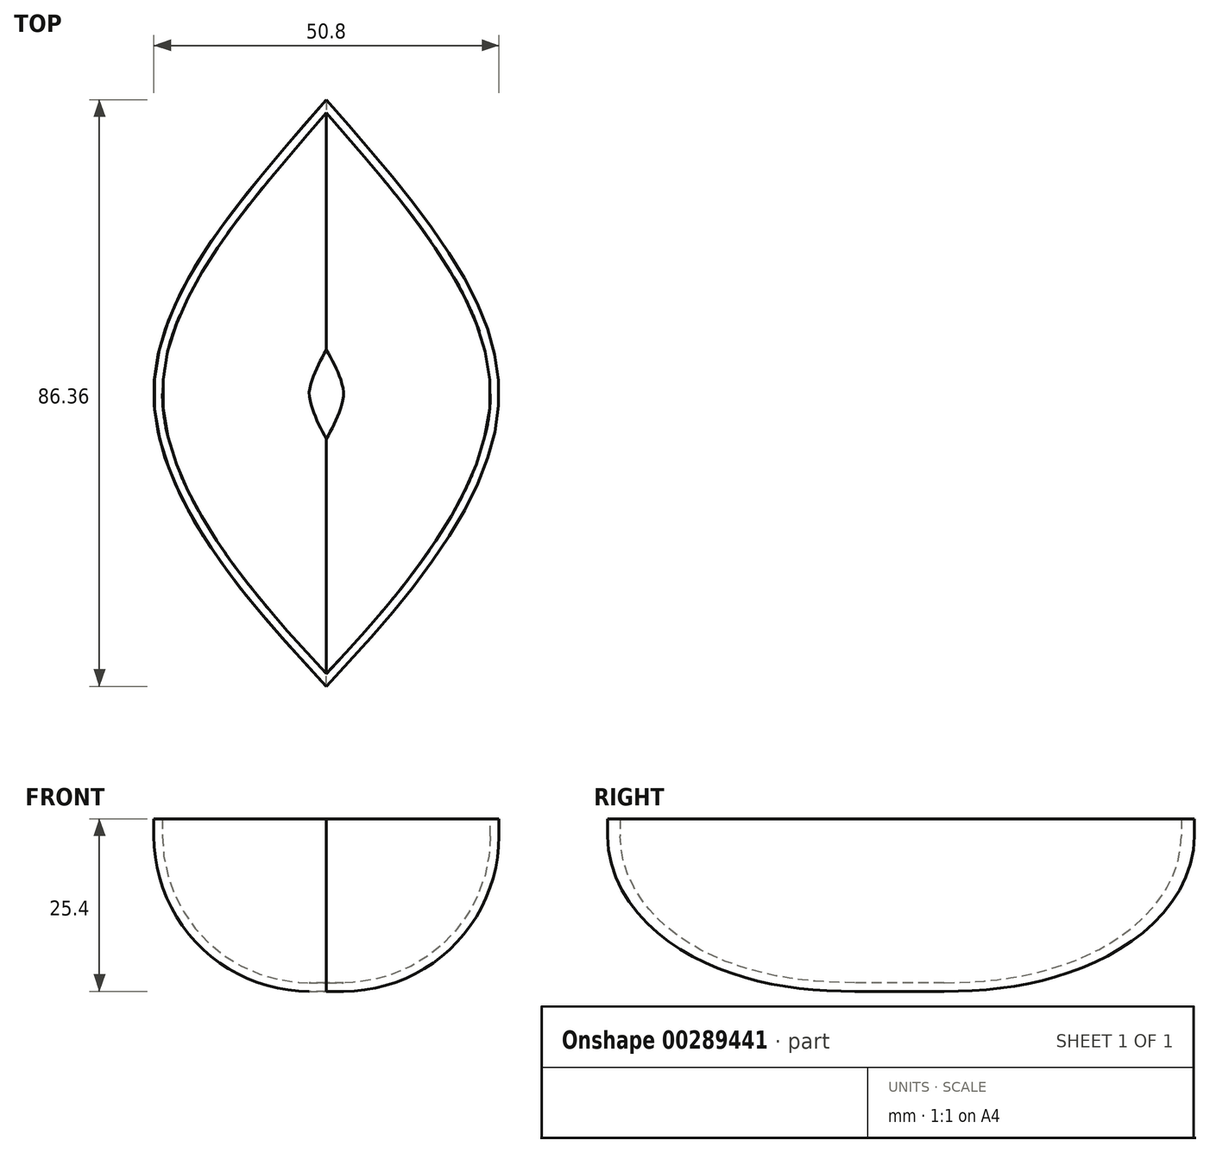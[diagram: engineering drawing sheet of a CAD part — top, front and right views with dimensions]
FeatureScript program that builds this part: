
annotation { "Feature Type Name" : "Feature", "Feature Type Description" : "" }
export const myFeature = defineFeature(function(context is Context, id is Id, definition is map)
    precondition{}
    {
        {
            var Q0;
            Q0=qCreatedBy(makeId("Top.planeOp"),FACE);
            var sketch = newSketch(context, id + "F0", { "sketchPlane" : qUnion([Q0])});
            skFitSpline(sketch, "E0", {"points": [v(0, 43.18) * mm, v(-25.4, 0) * mm, v(0, -43.18) * mm], "startDerivative": vector(-75.83, -87.8) * mm, "endDerivative": vector(76.6, -81.14) * mm});
            skFitSpline(sketch, "E1", {"points": [v(0, 43.18) * mm, v(25.4, 0) * mm, v(0, -43.18) * mm], "startDerivative": vector(75.77, -87.8) * mm, "endDerivative": vector(-76.54, -81.14) * mm});
            skSolve(sketch);
        }
        {
            var Q0;
            Q0=makeQuery(id+"F0.imprint","IMPRINT",FACE,{"disambiguationData":[TD([[makeQuery(id+"F0.imprint","IMPRINT",EDGE,{"derivedFrom":sQuery(id+"F0.wireOp",EDGE,"E0")}),1.0]])]});
            extrude(context, id + "F1", {"entities" : qUnion([Q0]), "depth" : 25.4 * mm});
        }
        {
            var Q0;
            Q0=makeQuery(id+"F1.opExtrude","CAP_EDGE",EDGE,{"disambiguationData":[OSD([sQuery(id+"F0.wireOp",EDGE,"E1")])],"isStart":true});
            var Q1;
            Q1=makeQuery(id+"F1.opExtrude","CAP_EDGE",EDGE,{"disambiguationData":[OSD([sQuery(id+"F0.wireOp",EDGE,"E0")])],"isStart":true});
            fillet(context, id + "F2", {"entities" : qUnion([Q0, Q1]), "radius" : 22.86 * mm, "tangentPropagation" : true, "allowEdgeOverflow" : false});
        }
        {
            var Q0;
            Q0=makeQuery(id+"F1.opExtrude","CAP_FACE",FACE,{"disambiguationData":[OSD([sQuery(id+"F0.wireOp",EDGE,"E0"),sQuery(id+"F0.wireOp",EDGE,"E1")])],"isStart":false});
            shell(context, id + "F3", {"entities" : qUnion([Q0]), "thickness" : 1.27 * mm});
        }
    });
